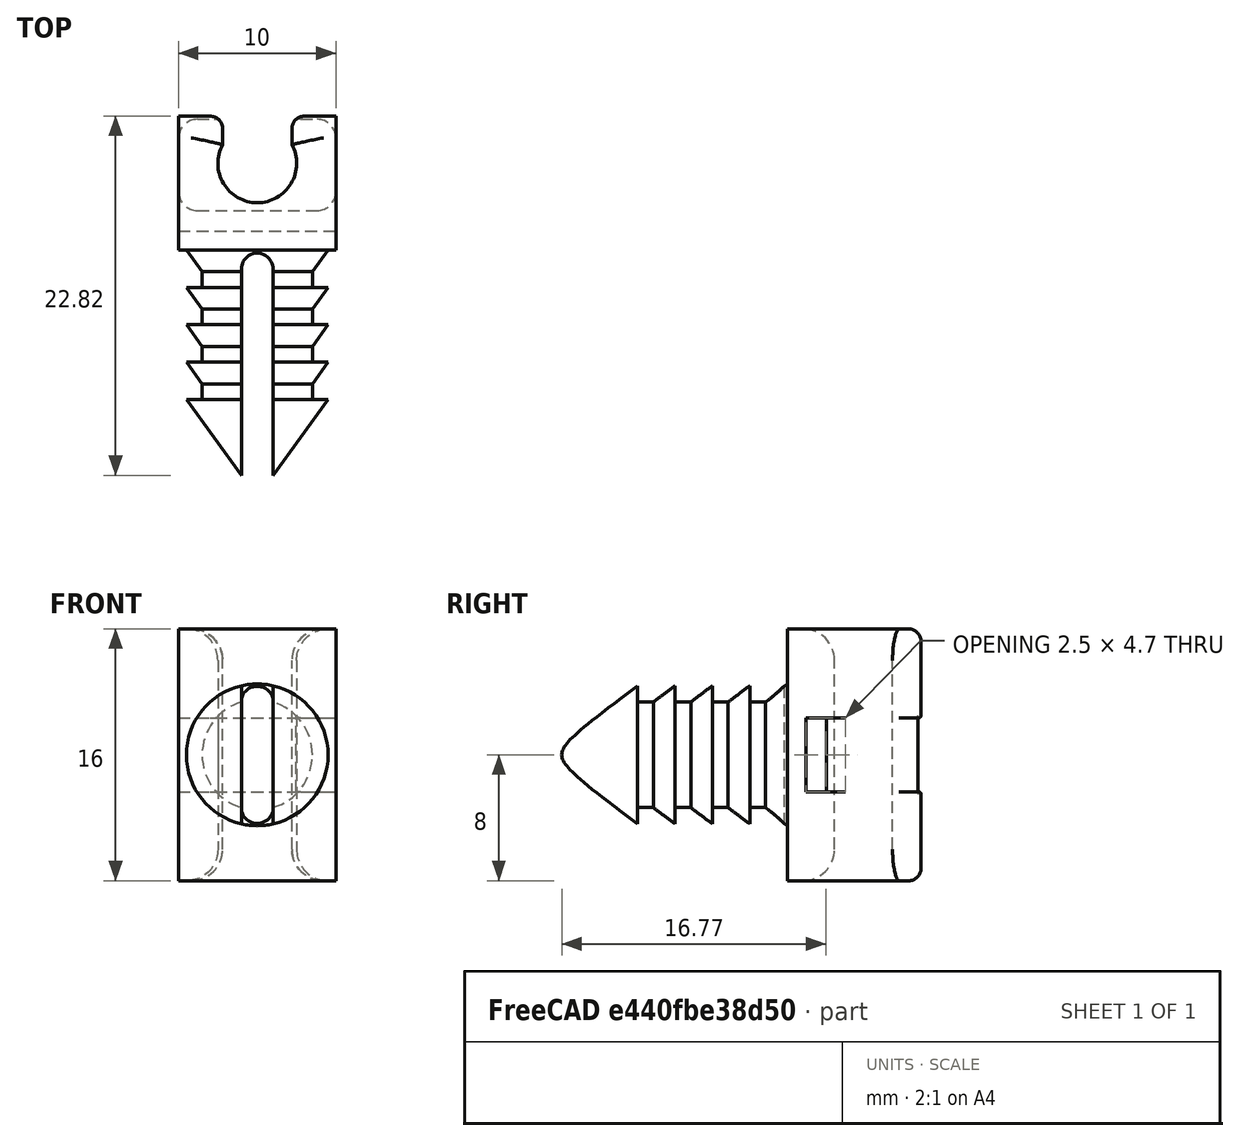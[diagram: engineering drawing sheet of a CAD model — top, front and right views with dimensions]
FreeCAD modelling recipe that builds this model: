
FCSTD DOCUMENT  (FreeCAD 0.21R33771 (Git))
Label: clip_brakes
License: All rights reserved
LicenseURL: http://en.wikipedia.org/wiki/All_rights_reserved
objects: Sketcher::SketchObject×4, PartDesign::Fillet×4, PartDesign::Body×3, PartDesign::Pad×2, PartDesign::Pocket×2, TechDraw::DrawViewDimension×2, Spreadsheet::Sheet×1, PartDesign::Revolution×1, PartDesign::LinearPattern×1, TechDraw::DrawSVGTemplate×1, PartDesign::Mirrored×1, Part::Cut×1, App::Part×1, TechDraw::DrawViewPart×1, TechDraw::DrawPage×1
note: 28 computed .brp shape members not serialized (recipe doc carries the construction recipe); baked Part::Feature solids carry a one-line shape summary decoded from their .brp

FEATURE [Spreadsheet::Sheet] Spreadsheet  label="parametres"
  cells = A1='Porte tuyau; D1='Rivet; G1='Fente du rivet; A2='largeur pièce; B2(holder_width)=10; D2='Rayon rivet; E2(rivet_radius)=3.5; G2='Epaisseur fente; H2(rivet_slot_thickness)=2; A3='Distance tuyau - base; B3(base_brake_line_distance)=3; D3='Rebord rivet; E3(rivet_edge)=1; G3='Longueur fente; H3(rivet_slot_length)=16; A4='epaisseur  piece; B4(extrusion_thickness)=16; D4='Longueur fleche rivet; E4(rivet_arrow_length)=6.2; A5='diamètre tuyau cuivre; B5(brake_line_diameter)=5; D5='Longueur rivet; E5(rivet_length)=9.5; A6='Restriction tuyau frein; B6(brake_line_restriction)=0.3; D6='Nombre de crans; E6(rivet_notches_number)=5; A7='Largeur serflex; B7(serflex_width)=4.7; D7='Distance inter-crans (calculée); E7==rivet_length / (rivet_notches_number - 1); A8='Epaisseur serflex; B8(serflex_thickness)=1.3
FEATURE [Sketcher::SketchObject] Sketch  label="Sketch_pipe_holder"
  FullyConstrained = true
  MapMode = 5
  Support = -> [XY_Plane]
  expr: Constraints[15] = <<parametres>>.base_brake_line_distance
  expr: Constraints[16] = <<parametres>>.brake_line_diameter / 2 + 0.5
  expr: Constraints[17] = <<parametres>>.brake_line_diameter / 2 - <<parametres>>.brake_line_restriction
  expr: Constraints[7] = <<parametres>>.brake_line_diameter / 2
  expr: Constraints[8] = <<parametres>>.holder_width / 2
  sketch-geometry (6):
    g0: LineSegment StartX=-5e-16 StartY=0 StartZ=0 EndX=-5 EndY=0 EndZ=0
    g1: LineSegment StartX=-5 StartY=0 StartZ=0 EndX=-5 EndY=8.5 EndZ=0
    g2: ArcOfCircle CenterX=-5e-16 CenterY=5.5 CenterZ=0 NormalX=0 NormalY=0 NormalZ=1 AngleXU=0 Radius=2.5 StartAngle=2.64666 EndAngle=4.71239
    g3: LineSegment StartX=-5e-16 StartY=3 StartZ=0 EndX=-5e-16 EndY=0 EndZ=0
    g4: LineSegment StartX=-5 StartY=8.5 StartZ=0 EndX=-2.2 EndY=8.5 EndZ=0
    g5: LineSegment StartX=-2.2 StartY=8.5 StartZ=0 EndX=-2.2 EndY=6.68743 EndZ=0
  constraints (18):
    c: Coincident(g0,g-1)
    c: PointOnObject(g0,g-1)
    c: Coincident(g1,g0)
    c: Vertical(g1)
    c: Coincident(g3,g2)
    c: Coincident(g3,g0)
    c: Vertical(g3)
    c: Radius(g2) = 2.5
    c: DistanceX(g1,g2) = 5
    c: Vertical(g2,g2)
    c: Coincident(g4,g1)
    c: Horizontal(g4)
    c: Coincident(g5,g4)
    c: Coincident(g5,g2)
    c: Vertical(g5)
    c: DistanceY(g0,g2) = 3
    c: DistanceY(g2,g4) = 3
    c: DistanceX(g2,g2) = 2.2
FEATURE [PartDesign::Pad] Pad
  Direction = (0,0,1)
  Length = 16
  Length2 = 10
  Midplane = true
  Profile = -> Sketch
  ReferenceAxis = -> Sketch [N_Axis]
  Type = 0
  expr: Length = <<parametres>>.extrusion_thickness
FEATURE [Sketcher::SketchObject] Sketch002  label="sketch_rivet"
  FullyConstrained = true
  MapMode = 5
  Support = -> [XY_Plane002]
  expr: Constraints[14] = <<parametres>>.rivet_arrow_length
  expr: Constraints[1] = <<parametres>>.rivet_edge
  expr: Constraints[3] = <<parametres>>.rivet_radius
  sketch-geometry (5):
    g0: LineSegment StartX=3.5 StartY=2 StartZ=0 EndX=0 EndY=2 EndZ=0
    g1: LineSegment StartX=4.5 StartY=0 StartZ=0 EndX=0 EndY=-6.2 EndZ=0
    g2: LineSegment StartX=0 StartY=-6.2 StartZ=0 EndX=0 EndY=2 EndZ=0
    g3: LineSegment StartX=3.5 StartY=0 StartZ=0 EndX=4.5 EndY=0 EndZ=0
    g4: LineSegment StartX=3.5 StartY=0 StartZ=0 EndX=3.5 EndY=2 EndZ=0
  constraints (16):
    c: Horizontal(g0)
    c: DistanceX(g0,g1) = 1
    c: PointOnObject(g1,g-2)
    c: DistanceX(g-1,g0) = 3.5
    c: PointOnObject(g0,g-2)
    c: Coincident(g2,g1)
    c: PointOnObject(g2,g0)
    c: Vertical(g2)
    c: Coincident(g4,g3)
    c: Coincident(g4,g0)
    c: Vertical(g4)
    c: Horizontal(g3)
    c: Coincident(g3,g1)
    c: DistanceY(g4,g4) = 2
    c: DistanceY(g1,g1) = 6.2
    c: PointOnObject(g1,g-1)
FEATURE [PartDesign::Revolution] Revolution  label="rivet001"
  Angle = 360
  Axis = (0,1,0)
  Base = (0,0,0)
  Profile = -> Sketch002
  ReferenceAxis = -> Sketch002 [V_Axis]
FEATURE [Sketcher::SketchObject] Sketch003  label="sketch_fente_rivet"
  FullyConstrained = true
  MapMode = 5
  Support = -> [XY_Plane003]
  expr: Constraints[6] = Spreadsheet.rivet_slot_thickness / 2
  expr: Constraints[7] = <<parametres>>.rivet_slot_length
  sketch-geometry (4):
    g0: ArcOfCircle CenterX=0 CenterY=-1.2 CenterZ=0 NormalX=0 NormalY=0 NormalZ=1 AngleXU=0 Radius=1 StartAngle=1.0666e-12 EndAngle=3.14159
    g1: ArcOfCircle CenterX=-3.82e-14 CenterY=-17.2 CenterZ=0 NormalX=0 NormalY=0 NormalZ=1 AngleXU=0 Radius=1 StartAngle=3.14159 EndAngle=6.28319
    g2: LineSegment StartX=-1 StartY=-1.2 StartZ=0 EndX=-1 EndY=-17.2 EndZ=0
    g3: LineSegment StartX=1 StartY=-17.2 StartZ=0 EndX=1 EndY=-1.2 EndZ=0
  constraints (10):
    c: Tangent(g0,g2) = -1.5708
    c: Tangent(g2,g1) = -1.5708
    c: Tangent(g1,g3) = -1.5708
    c: Tangent(g3,g0) = -1.5708
    c: Equal(g0,g1)
    c: Vertical(g2)
    c: DistanceX(g1,g1) = 1
    c: DistanceY(g1,g0) = 16
    c: DistanceX(g0,g-1) = 0
    c: DistanceY(g0,g-1) = 1.2
FEATURE [PartDesign::Pad] Pad001  label="vide_rivet"
  Direction = (0,0,1)
  Length = 11
  Length2 = 10
  Midplane = true
  Profile = -> Sketch003
  ReferenceAxis = -> Sketch003 [N_Axis]
  Type = 0
FEATURE [PartDesign::Body] Body002  label="vide rivet"
  Group = -> [Sketch003,Pad001]
  Origin = -> Origin003
  Tip = -> Pad001
FEATURE [PartDesign::LinearPattern] LinearPattern
  BaseFeature = -> Revolution
  Direction = -> Sketch002 [V_Axis]
  Length = 9.5
  Occurrences = 5
  Originals = -> [Revolution]
  Reversed = true
  expr: Length = <<parametres>>.rivet_length
  expr: Occurrences = <<parametres>>.rivet_notches_number
FEATURE [TechDraw::DrawSVGTemplate] Template
  EditableTexts = Designed_by_Name=Guigui; Drawing_number=Drawing number; FC-Date=Date; FC-SC=Scale; FC-SH=Sheet; FC-Title=Defender fuel pipe clip; Subtitle=Subtitle; Weight=Weight
  Height = 210
  Orientation = 1
  Width = 297
FEATURE [PartDesign::Mirrored] Mirrored
  BaseFeature = -> Pad
  MirrorPlane = -> Sketch [V_Axis]
  Originals = -> [Pad]
FEATURE [PartDesign::Fillet] Fillet
  Base = -> Mirrored [Edge23,Edge24,Edge13,Edge12,Edge16,Edge17,Edge27,Edge26]
  BaseFeature = -> Mirrored
  Radius = 2
  SupportTransform = false
  UseAllEdges = false
FEATURE [PartDesign::Fillet] Fillet001
  Base = -> Fillet [Edge37,Edge7]
  BaseFeature = -> Fillet
  Radius = 0.8
  SupportTransform = false
  UseAllEdges = false
FEATURE [Sketcher::SketchObject] Sketch004  label="trou_serflex"
  FullyConstrained = true
  MapMode = 5
  Placement = pos=(-5,0,0) rot=(0.57735,-0.57735,-0.57735;2.0944rad)
  Support = -> [Mirrored]
  expr: Constraints[11] = <<parametres>>.serflex_width / 2
  expr: Constraints[20] = <<parametres>>.serflex_width
  expr: Constraints[22] = <<parametres>>.serflex_width / 2
  expr: Constraints[8] = <<parametres>>.serflex_thickness
  expr: Constraints[9] = <<parametres>>.serflex_width
  sketch-geometry (8):
    g0: LineSegment StartX=-2.5 StartY=2.35 StartZ=0 EndX=-1.2 EndY=2.35 EndZ=0
    g1: LineSegment StartX=-1.2 StartY=2.35 StartZ=0 EndX=-1.2 EndY=-2.35 EndZ=0
    g2: LineSegment StartX=-1.2 StartY=-2.35 StartZ=0 EndX=-2.5 EndY=-2.35 EndZ=0
    g3: LineSegment StartX=-2.5 StartY=-2.35 StartZ=0 EndX=-2.5 EndY=2.35 EndZ=0
    g4: LineSegment StartX=-8.5 StartY=2.35 StartZ=0 EndX=-8.3 EndY=2.35 EndZ=0
    g5: LineSegment StartX=-8.3 StartY=2.35 StartZ=0 EndX=-8.3 EndY=-2.35 EndZ=0
    g6: LineSegment StartX=-8.3 StartY=-2.35 StartZ=0 EndX=-8.5 EndY=-2.35 EndZ=0
    g7: LineSegment StartX=-8.5 StartY=-2.35 StartZ=0 EndX=-8.5 EndY=2.35 EndZ=0
  constraints (24):
    c: Coincident(g0,g1)
    c: Coincident(g1,g2)
    c: Coincident(g2,g3)
    c: Coincident(g3,g0)
    c: Horizontal(g0)
    c: Horizontal(g2)
    c: Vertical(g1)
    c: Vertical(g3)
    c: DistanceX(g0,g0) = 1.3
    c: DistanceY(g3,g3) = 4.7
    c: DistanceX(g0,g-1) = 1.2
    c: DistanceY(g-1,g0) = 2.35
    c: Coincident(g4,g5)
    c: Coincident(g5,g6)
    c: Coincident(g6,g7)
    c: Coincident(g7,g4)
    c: Horizontal(g4)
    c: Horizontal(g6)
    c: Vertical(g5)
    c: Vertical(g7)
    c: DistanceY(g7,g7) = 4.7
    c: DistanceX(g4,g4) = 0.2
    c: DistanceY(g-1,g4) = 2.35
    c: DistanceX(g4,g-1) = 8.3
FEATURE [PartDesign::Pocket] Pocket001  label="truncation_rivet"
  BaseFeature = -> LinearPattern
  Direction = (0,-1,0)
  Length = 2
  Length2 = 5
  Profile = -> LinearPattern [Face3]
  Type = 0
FEATURE [PartDesign::Body] Body001  label="rivet"
  Group = -> [Sketch002,Revolution,LinearPattern,Pocket001]
  Origin = -> Origin002
  Tip = -> Pocket001
FEATURE [Part::Cut] Cut
  Base = -> Body001
  Tool = -> Body002
FEATURE [PartDesign::Pocket] Pocket
  BaseFeature = -> Fillet001
  Direction = (1,0,0)
  Length = 10
  Length2 = 5
  Profile = -> Sketch004
  ReferenceAxis = -> Sketch004 [N_Axis]
  Type = 0
  expr: Length = <<parametres>>.holder_width
FEATURE [PartDesign::Fillet] Fillet002
  Base = -> Pocket [Edge17,Edge23,Edge74,Edge61]
  BaseFeature = -> Pocket
  Radius = 1.2
  SupportTransform = false
  UseAllEdges = false
FEATURE [PartDesign::Fillet] Fillet003
  Base = -> Fillet002 [Edge30,Edge22,Edge121,Edge114]
  BaseFeature = -> Fillet002
  Radius = 0.15
  SupportTransform = false
  UseAllEdges = false
FEATURE [PartDesign::Body] Body  label="pipe_holders"
  Group = -> [Sketch,Pad,Mirrored,Fillet,Fillet001,Sketch004,Pocket,Fillet002,Fillet003]
  Origin = -> Origin
  Tip = -> Fillet003
FEATURE [App::Part] Part  label="fuel_pipe_clip"
  Group = -> [Body,Body001,Body002]
  Origin = -> Origin001
FEATURE [TechDraw::DrawViewPart] View
  CoarseView = false
  Direction = (0,0,1)
  Focus = 100
  HardHidden = false
  IsoCount = 0
  IsoHidden = false
  IsoVisible = false
  LockPosition = false
  Perspective = false
  Rotation = 0
  Scale = 5
  ScaleType = 0
  ScrubCount = 0
  SeamHidden = false
  SeamVisible = true
  SmoothHidden = false
  SmoothVisible = true
  Source = -> [Cut,Body,Body001,Body002,Origin,Pad,Mirrored,X_Axis,Y_Axis,Z_Axis,XY_Plane,XZ_Plane,YZ_Plane,Sketch,Origin002,Revolution,LinearPattern,Sketch002,Origin003,Pad001,Sketch003]
  X = 109.229
  XDirection = (1,0,0)
  Y = 116.196
FEATURE [TechDraw::DrawViewDimension] Dimension001
  AngleOverride = false
  Arbitrary = false
  ArbitraryTolerances = false
  EqualTolerance = true
  ExtensionAngle = 0
  FormatSpec = %.2w
  FormatSpecOverTolerance = %+.2w
  FormatSpecUnderTolerance = %+.2w
  Inverted = false
  LineAngle = 0
  LockPosition = false
  MeasureType = 1
  OverTolerance = 0
  References2D = -> [View]
  Rotation = 0
  Scale = 5
  ScaleType = 0
  TheoreticalExact = false
  Type = 2
  UnderTolerance = 0
  X = 34.0688
  Y = 5.67301
FEATURE [TechDraw::DrawViewDimension] Dimension
  AngleOverride = false
  Arbitrary = false
  ArbitraryTolerances = false
  EqualTolerance = true
  ExtensionAngle = 0
  FormatSpec = %.2w
  FormatSpecOverTolerance = %+.2w
  FormatSpecUnderTolerance = %+.2w
  Inverted = false
  LineAngle = 0
  LockPosition = false
  MeasureType = 1
  OverTolerance = 0
  References2D = -> [View]
  Rotation = 0
  Scale = 5
  ScaleType = 0
  TheoreticalExact = false
  Type = 2
  UnderTolerance = 0
  X = -38.1592
  Y = 4.4472
FEATURE [TechDraw::DrawPage] Page
  KeepUpdated = true
  NextBalloonIndex = 1
  ProjectionType = 0
  Scale = 5
  Template = -> Template
  Views = -> [View,Dimension001,Dimension]
